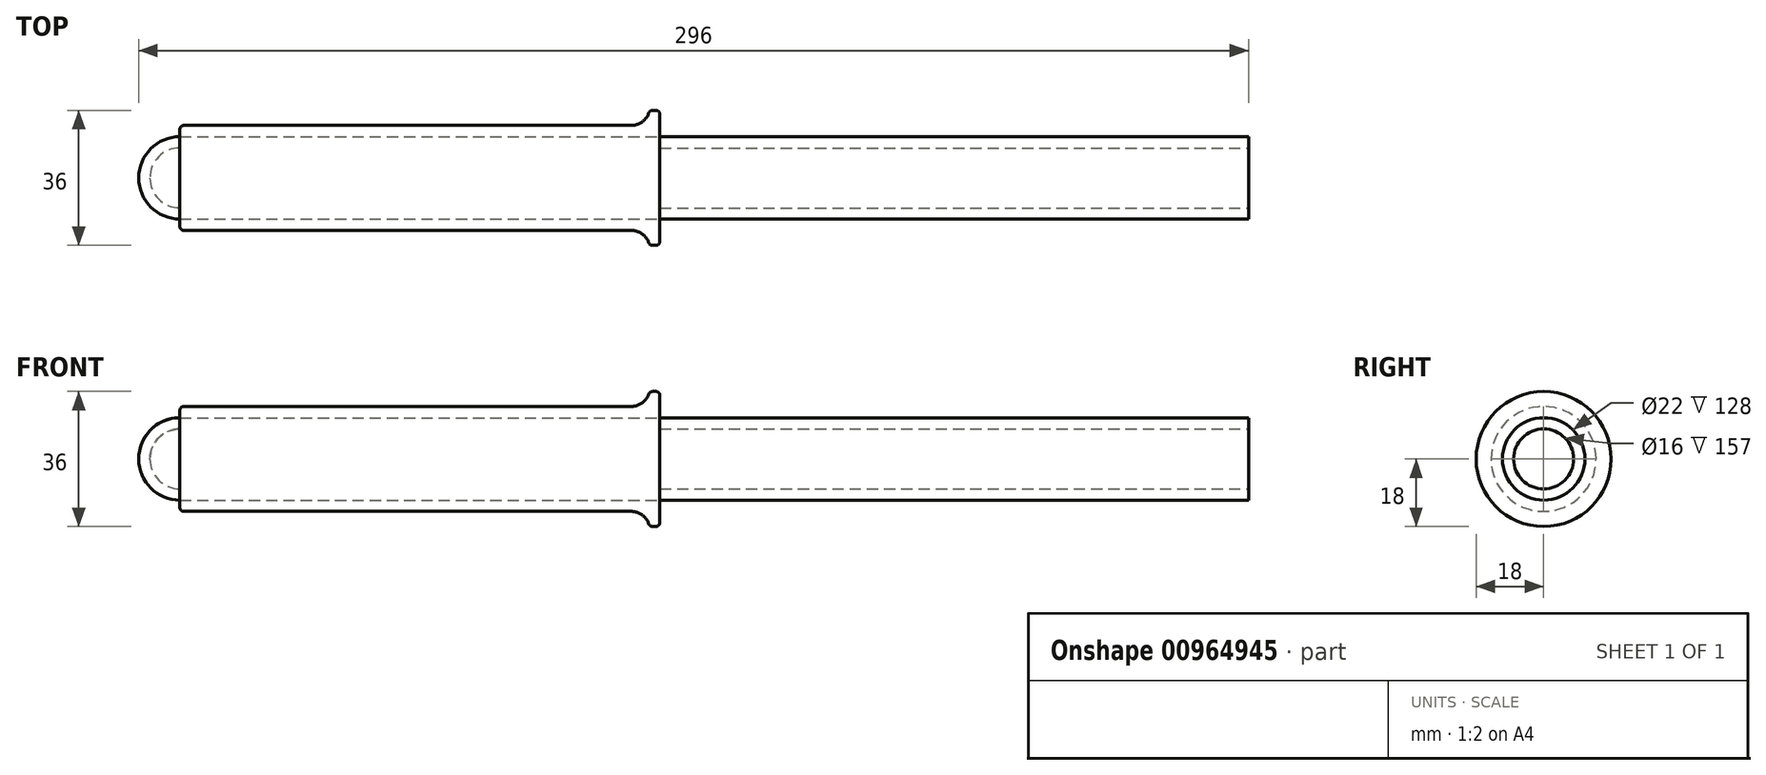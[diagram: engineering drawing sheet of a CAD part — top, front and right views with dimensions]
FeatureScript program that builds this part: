
annotation { "Feature Type Name" : "Feature", "Feature Type Description" : "" }
export const myFeature = defineFeature(function(context is Context, id is Id, definition is map)
    precondition{}
    {
        {
            var Q0;
            Q0=qCreatedBy(makeId("Front.planeOp"),FACE);
            var sketch = newSketch(context, id + "F0", { "sketchPlane" : qUnion([Q0])});
            skLineSegment(sketch, "E0", {"start": v(0, 0) * mm, "end": v(-296, 0) * mm});
            skLineSegment(sketch, "E1", {"start": v(0, 0) * mm, "end": v(0, 11) * mm});
            skPoint(sketch, "E2", {"position": v(-285, 0) * mm});
            skArc(sketch, "E3", {"start": v(-285, 11) * mm, "mid": v(-292.78, 7.78) * mm, "end": v(-296, 0) * mm});
            skLineSegment(sketch, "E4", {"start": v(0, 11) * mm, "end": v(-285, 11) * mm});
            skSolve(sketch);
        }
        {
            var Q0;
            Q0=makeQuery(id+"F0.imprint","IMPRINT",FACE,{"disambiguationData":[TD([[makeQuery(id+"F0.imprint","IMPRINT",EDGE,{"derivedFrom":sQuery(id+"F0.wireOp",EDGE,"E0")}),-1.0]])]});
            var Q1;
            Q1=sQuery(id+"F0.wireOp",EDGE,"E0");
            revolve(context, id + "F1", {"surfaceOperationType" : NewSurfaceOperationType.NEW, "entities" : qUnion([Q0]), "axis" : qUnion([Q1]), "revolveType" : RevolveType.FULL});
        }
        {
            var Q0;
            Q0=makeQuery(id+"F1.opRevolve","SWEPT_FACE",FACE,{"disambiguationData":[OSD([sQuery(id+"F0.wireOp",EDGE,"E1")])]});
            shell(context, id + "F2", {"entities" : qUnion([Q0]), "thickness" : 3 * mm});
        }
        {
            var Q0;
            Q0=qCreatedBy(makeId("Front.planeOp"),FACE);
            var sketch = newSketch(context, id + "F3", { "sketchPlane" : qUnion([Q0])});
            skLineSegment(sketch, "E5.0", {"start": v(-285, 11) * mm, "end": v(-285, -11) * mm, "construction": true});
            skLineSegment(sketch, "E6", {"start": v(-285, 0) * mm, "end": v(-285, 14) * mm});
            skLineSegment(sketch, "E7", {"start": v(-285, 14) * mm, "end": v(-160, 14) * mm});
            skLineSegment(sketch, "E8", {"start": v(-160, 14) * mm, "end": v(-160, 18) * mm});
            skLineSegment(sketch, "E9", {"start": v(-160, 18) * mm, "end": v(-157, 18) * mm});
            skLineSegment(sketch, "E10", {"start": v(-157, 18) * mm, "end": v(-157, 0) * mm});
            skLineSegment(sketch, "E11", {"start": v(-157, 0) * mm, "end": v(-285, 0) * mm});
            skSolve(sketch);
        }
        {
            var Q0;
            Q0=makeQuery(id+"F3.imprint","IMPRINT",FACE,{"disambiguationData":[TD([[makeQuery(id+"F3.imprint","IMPRINT",EDGE,{"derivedFrom":sQuery(id+"F3.wireOp",EDGE,"E6")}),-1.0]])]});
            var Q1;
            Q1=sQuery(id+"F3.wireOp",EDGE,"E11");
            revolve(context, id + "F4", {"surfaceOperationType" : NewSurfaceOperationType.NEW, "entities" : qUnion([Q0]), "axis" : qUnion([Q1]), "revolveType" : RevolveType.FULL});
        }
        {
            var Q0;
            Q0=makeQuery(id+"F4.opRevolve","SWEPT_FACE",FACE,{"disambiguationData":[OSD([sQuery(id+"F3.wireOp",EDGE,"E10")])]});
            var sketch = newSketch(context, id + "F5", { "sketchPlane" : qUnion([Q0])});
            skCircle(sketch, "E12.0", {"center": v(0, 0) * mm, "radius": 11 * mm});
            skSolve(sketch);
        }
        {
            var Q0;
            Q0=makeQuery(id+"F5.imprint","IMPRINT",FACE,{"disambiguationData":[TD([[makeQuery(id+"F5.imprint","IMPRINT",EDGE,{"derivedFrom":sQuery(id+"F5.wireOp",EDGE,"E12.0")}),1.0]])]});
            extrude(context, id + "F6", {"entities" : qUnion([Q0]), "operationType" : NewBodyOperationType.REMOVE, "endBound" : BoundingType.UP_TO_NEXT, "oppositeDirection" : true, "depth" : 25 * mm, "offsetDistance" : 25 * mm});
        }
        {
            var Q0;
            Q0=makeQuery(id+"F4.opRevolve","SWEPT_EDGE",EDGE,{"disambiguationData":[OSD([sQuery(id+"F3.wireOp",EDGE,"E6"),sQuery(id+"F3.wireOp",EDGE,"E7")])]});
            var Q1;
            Q1=makeQuery(id+"F4.opRevolve","SWEPT_FACE",FACE,{"disambiguationData":[OSD([sQuery(id+"F3.wireOp",EDGE,"E9")])]});
            fillet(context, id + "F7", {"entities" : qUnion([Q0, Q1]), "radius" : 1 * mm, "tangentPropagation" : true, "allowEdgeOverflow" : false});
        }
        {
            var Q0;
            Q0=makeQuery(id+"F4.opRevolve","SWEPT_EDGE",EDGE,{"disambiguationData":[OSD([sQuery(id+"F3.wireOp",EDGE,"E7"),sQuery(id+"F3.wireOp",EDGE,"E8")])]});
            fillet(context, id + "F8", {"entities" : qUnion([Q0]), "radius" : 5 * mm, "tangentPropagation" : true, "allowEdgeOverflow" : false});
        }
    });
